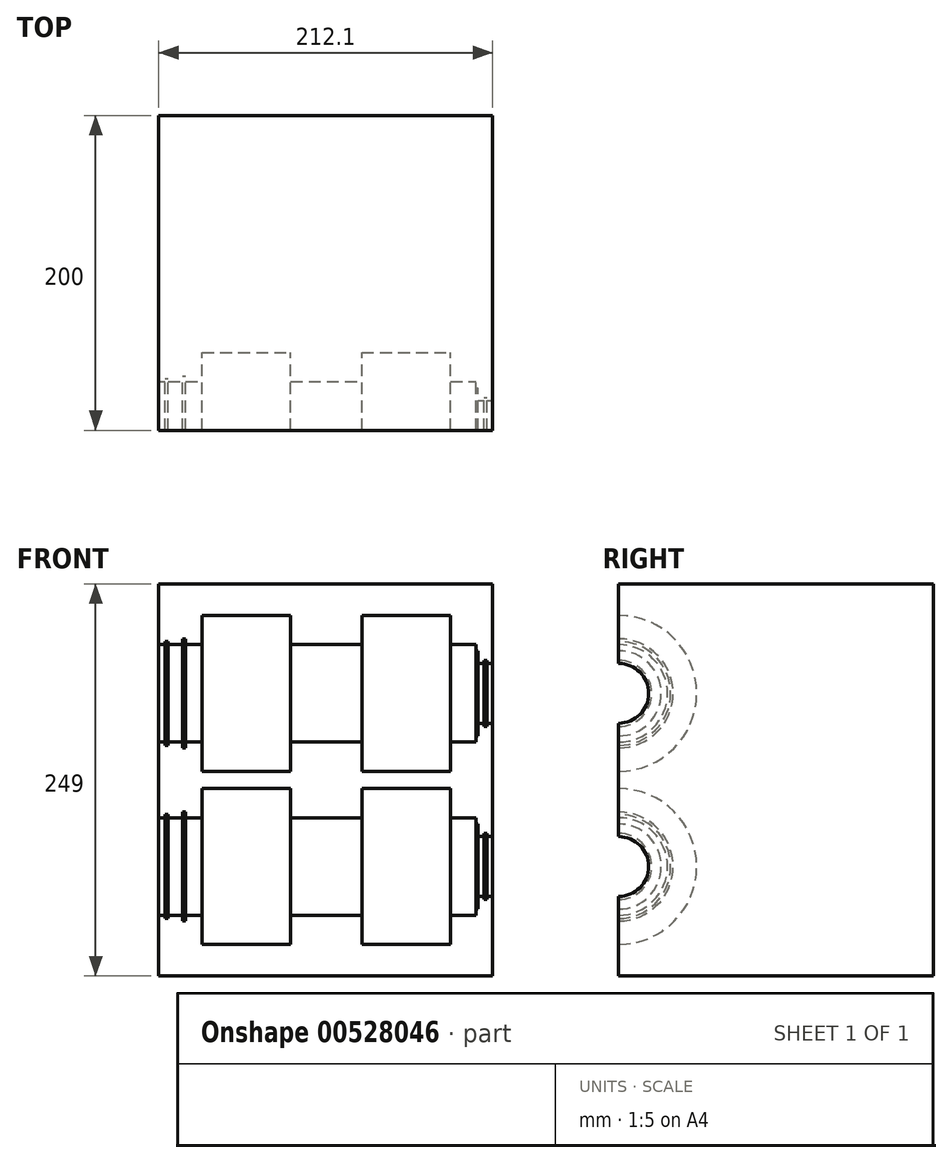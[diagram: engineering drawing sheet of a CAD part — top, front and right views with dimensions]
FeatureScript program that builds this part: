
annotation { "Feature Type Name" : "Feature", "Feature Type Description" : "" }
export const myFeature = defineFeature(function(context is Context, id is Id, definition is map)
    precondition{}
    {
        {
            var Q0;
            Q0=qCreatedBy(makeId("Front.planeOp"),FACE);
            var sketch = newSketch(context, id + "F0", { "sketchPlane" : qUnion([Q0])});
            skLineSegment(sketch, "E0", {"start": v(-107.72, -38.68) * mm, "end": v(-103.72, -38.68) * mm});
            skLineSegment(sketch, "E1", {"start": v(-103.72, -38.68) * mm, "end": v(-103.72, -36.68) * mm});
            skLineSegment(sketch, "E2", {"start": v(-103.72, -36.68) * mm, "end": v(-101.72, -36.68) * mm});
            skLineSegment(sketch, "E3", {"start": v(-101.72, -36.68) * mm, "end": v(-101.72, -38.68) * mm});
            skLineSegment(sketch, "E4", {"start": v(-101.72, -38.68) * mm, "end": v(-92.72, -38.68) * mm});
            skLineSegment(sketch, "E5", {"start": v(-92.72, -38.68) * mm, "end": v(-92.72, -35.08) * mm});
            skLineSegment(sketch, "E6", {"start": v(-92.72, -35.08) * mm, "end": v(-90.72, -35.08) * mm});
            skLineSegment(sketch, "E7", {"start": v(-90.72, -35.08) * mm, "end": v(-90.72, -38.68) * mm});
            skLineSegment(sketch, "E8", {"start": v(-90.72, -38.68) * mm, "end": v(-80.22, -38.68) * mm});
            skLineSegment(sketch, "E9", {"start": v(-80.22, -38.68) * mm, "end": v(-80.22, -20.18) * mm});
            skLineSegment(sketch, "E10", {"start": v(-80.22, -20.18) * mm, "end": v(-23.92, -20.18) * mm});
            skLineSegment(sketch, "E11", {"start": v(-23.92, -20.18) * mm, "end": v(-23.92, -38.68) * mm});
            skLineSegment(sketch, "E12", {"start": v(-23.92, -38.68) * mm, "end": v(21.28, -38.68) * mm});
            skLineSegment(sketch, "E13", {"start": v(21.28, -38.68) * mm, "end": v(21.28, -20.18) * mm});
            skLineSegment(sketch, "E14", {"start": v(21.28, -20.18) * mm, "end": v(77.58, -20.18) * mm});
            skLineSegment(sketch, "E15", {"start": v(77.58, -20.18) * mm, "end": v(77.58, -38.68) * mm});
            skLineSegment(sketch, "E16", {"start": v(77.58, -38.68) * mm, "end": v(93.88, -38.68) * mm});
            skLineSegment(sketch, "E17", {"start": v(93.88, -38.68) * mm, "end": v(93.88, -42.68) * mm});
            skLineSegment(sketch, "E18", {"start": v(93.88, -42.68) * mm, "end": v(94.88, -42.68) * mm});
            skLineSegment(sketch, "E19", {"start": v(94.88, -42.68) * mm, "end": v(94.88, -50.68) * mm});
            skLineSegment(sketch, "E20", {"start": v(94.88, -50.68) * mm, "end": v(98.88, -50.68) * mm});
            skLineSegment(sketch, "E21", {"start": v(98.88, -50.68) * mm, "end": v(98.88, -48.68) * mm});
            skLineSegment(sketch, "E22", {"start": v(98.88, -48.68) * mm, "end": v(100.88, -48.68) * mm});
            skLineSegment(sketch, "E23", {"start": v(100.88, -48.68) * mm, "end": v(100.88, -50.68) * mm});
            skLineSegment(sketch, "E24", {"start": v(100.88, -50.68) * mm, "end": v(104.38, -50.68) * mm});
            skLineSegment(sketch, "E25", {"start": v(-107.72, -69.68) * mm, "end": v(104.38, -69.68) * mm});
            skLineSegment(sketch, "E26", {"start": v(-107.72, 71.32) * mm, "end": v(-103.72, 71.32) * mm});
            skLineSegment(sketch, "E27", {"start": v(-103.72, 71.32) * mm, "end": v(-103.72, 73.32) * mm});
            skLineSegment(sketch, "E28", {"start": v(-103.72, 73.32) * mm, "end": v(-101.72, 73.32) * mm});
            skLineSegment(sketch, "E29", {"start": v(-101.72, 73.32) * mm, "end": v(-101.72, 71.32) * mm});
            skLineSegment(sketch, "E30", {"start": v(-101.72, 71.32) * mm, "end": v(-92.72, 71.32) * mm});
            skLineSegment(sketch, "E31", {"start": v(-92.72, 71.32) * mm, "end": v(-92.72, 74.92) * mm});
            skLineSegment(sketch, "E32", {"start": v(-92.72, 74.92) * mm, "end": v(-90.72, 74.92) * mm});
            skLineSegment(sketch, "E33", {"start": v(-90.72, 74.92) * mm, "end": v(-90.72, 71.32) * mm});
            skLineSegment(sketch, "E34", {"start": v(-90.72, 71.32) * mm, "end": v(-80.22, 71.32) * mm});
            skLineSegment(sketch, "E35", {"start": v(-80.22, 71.32) * mm, "end": v(-80.22, 89.82) * mm});
            skLineSegment(sketch, "E36", {"start": v(-80.22, 89.82) * mm, "end": v(-23.92, 89.82) * mm});
            skLineSegment(sketch, "E37", {"start": v(-23.92, 89.82) * mm, "end": v(-23.92, 71.32) * mm});
            skLineSegment(sketch, "E38", {"start": v(-23.92, 71.32) * mm, "end": v(21.28, 71.32) * mm});
            skLineSegment(sketch, "E39", {"start": v(21.28, 71.32) * mm, "end": v(21.28, 89.82) * mm});
            skLineSegment(sketch, "E40", {"start": v(21.28, 89.82) * mm, "end": v(77.58, 89.82) * mm});
            skLineSegment(sketch, "E41", {"start": v(77.58, 89.82) * mm, "end": v(77.58, 71.32) * mm});
            skLineSegment(sketch, "E42", {"start": v(77.58, 71.32) * mm, "end": v(93.88, 71.32) * mm});
            skLineSegment(sketch, "E43", {"start": v(93.88, 71.32) * mm, "end": v(93.88, 67.32) * mm});
            skLineSegment(sketch, "E44", {"start": v(93.88, 67.32) * mm, "end": v(94.88, 67.32) * mm});
            skLineSegment(sketch, "E45", {"start": v(94.88, 67.32) * mm, "end": v(94.88, 59.32) * mm});
            skLineSegment(sketch, "E46", {"start": v(94.88, 59.32) * mm, "end": v(98.88, 59.32) * mm});
            skLineSegment(sketch, "E47", {"start": v(98.88, 59.32) * mm, "end": v(98.88, 61.32) * mm});
            skLineSegment(sketch, "E48", {"start": v(98.88, 61.32) * mm, "end": v(100.88, 61.32) * mm});
            skLineSegment(sketch, "E49", {"start": v(100.88, 61.32) * mm, "end": v(100.88, 59.32) * mm});
            skLineSegment(sketch, "E50", {"start": v(100.88, 59.32) * mm, "end": v(104.38, 59.32) * mm});
            skLineSegment(sketch, "E51", {"start": v(-107.72, 40.32) * mm, "end": v(104.38, 40.32) * mm});
            skLineSegment(sketch, "E52", {"start": v(-107.72, 71.32) * mm, "end": v(-107.72, 40.32) * mm});
            skLineSegment(sketch, "E53", {"start": v(104.38, 40.32) * mm, "end": v(104.38, 59.32) * mm});
            skLineSegment(sketch, "E54", {"start": v(-107.72, -69.68) * mm, "end": v(-107.72, -38.68) * mm});
            skLineSegment(sketch, "E55", {"start": v(104.38, -69.68) * mm, "end": v(104.38, -50.68) * mm});
            skLineSegment(sketch, "E56", {"start": v(-107.72, 109.82) * mm, "end": v(104.38, 109.82) * mm});
            skLineSegment(sketch, "E57.MirrorCS", {"start": v(-103.72, 7.32) * mm, "end": v(-101.72, 7.32) * mm});
            skLineSegment(sketch, "E58.MirrorCS", {"start": v(98.88, 19.32) * mm, "end": v(100.88, 19.32) * mm});
            skLineSegment(sketch, "E59.MirrorCS", {"start": v(98.88, 21.32) * mm, "end": v(98.88, 19.32) * mm});
            skLineSegment(sketch, "E60.MirrorCS", {"start": v(93.88, 13.32) * mm, "end": v(94.88, 13.32) * mm});
            skLineSegment(sketch, "E61.MirrorCS", {"start": v(-103.72, 9.32) * mm, "end": v(-103.72, 7.32) * mm});
            skLineSegment(sketch, "E62.MirrorCS", {"start": v(93.88, 9.32) * mm, "end": v(93.88, 13.32) * mm});
            skLineSegment(sketch, "E63.MirrorCS", {"start": v(-101.72, 7.32) * mm, "end": v(-101.72, 9.32) * mm});
            skLineSegment(sketch, "E64.MirrorCS", {"start": v(100.88, 21.32) * mm, "end": v(104.38, 21.32) * mm});
            skLineSegment(sketch, "E65.MirrorCS", {"start": v(-92.72, 5.72) * mm, "end": v(-90.72, 5.72) * mm});
            skLineSegment(sketch, "E66.MirrorCS", {"start": v(100.88, 19.32) * mm, "end": v(100.88, 21.32) * mm});
            skLineSegment(sketch, "E67.MirrorCS", {"start": v(-90.72, 5.72) * mm, "end": v(-90.72, 9.32) * mm});
            skLineSegment(sketch, "E68.MirrorCS", {"start": v(-107.72, 9.32) * mm, "end": v(-103.72, 9.32) * mm});
            skLineSegment(sketch, "E69.MirrorCS", {"start": v(94.88, 21.32) * mm, "end": v(98.88, 21.32) * mm});
            skLineSegment(sketch, "E70.MirrorCS", {"start": v(-101.72, 9.32) * mm, "end": v(-92.72, 9.32) * mm});
            skLineSegment(sketch, "E71.MirrorCS", {"start": v(-92.72, 9.32) * mm, "end": v(-92.72, 5.72) * mm});
            skLineSegment(sketch, "E72.MirrorCS", {"start": v(-90.72, 9.32) * mm, "end": v(-80.22, 9.32) * mm});
            skLineSegment(sketch, "E73.MirrorCS", {"start": v(94.88, 13.32) * mm, "end": v(94.88, 21.32) * mm});
            skLineSegment(sketch, "E74.MirrorCS", {"start": v(21.28, 9.32) * mm, "end": v(21.28, -9.18) * mm});
            skLineSegment(sketch, "E75.MirrorCS", {"start": v(-23.92, 9.32) * mm, "end": v(21.28, 9.32) * mm});
            skLineSegment(sketch, "E76.MirrorCS", {"start": v(77.58, 9.32) * mm, "end": v(93.88, 9.32) * mm});
            skLineSegment(sketch, "E77.MirrorCS", {"start": v(-80.22, -9.18) * mm, "end": v(-23.92, -9.18) * mm});
            skLineSegment(sketch, "E78.MirrorCS", {"start": v(-80.22, 9.32) * mm, "end": v(-80.22, -9.18) * mm});
            skLineSegment(sketch, "E79.MirrorCS", {"start": v(-23.92, -9.18) * mm, "end": v(-23.92, 9.32) * mm});
            skLineSegment(sketch, "E80.MirrorCS", {"start": v(77.58, -9.18) * mm, "end": v(77.58, 9.32) * mm});
            skLineSegment(sketch, "E81.MirrorCS", {"start": v(21.28, -9.18) * mm, "end": v(77.58, -9.18) * mm});
            skLineSegment(sketch, "E82", {"start": v(-107.72, 9.32) * mm, "end": v(-107.72, 40.32) * mm});
            skLineSegment(sketch, "E83", {"start": v(104.38, 21.32) * mm, "end": v(104.38, 40.32) * mm});
            skLineSegment(sketch, "E84.MirrorCS", {"start": v(94.88, -96.68) * mm, "end": v(94.88, -88.68) * mm});
            skLineSegment(sketch, "E85.MirrorCS", {"start": v(-92.72, -104.28) * mm, "end": v(-90.72, -104.28) * mm});
            skLineSegment(sketch, "E86.MirrorCS", {"start": v(98.88, -90.68) * mm, "end": v(100.88, -90.68) * mm});
            skLineSegment(sketch, "E87.MirrorCS", {"start": v(94.88, -88.68) * mm, "end": v(98.88, -88.68) * mm});
            skLineSegment(sketch, "E88.MirrorCS", {"start": v(100.88, -90.68) * mm, "end": v(100.88, -88.68) * mm});
            skLineSegment(sketch, "E89.MirrorCS", {"start": v(100.88, -88.68) * mm, "end": v(104.38, -88.68) * mm});
            skLineSegment(sketch, "E90.MirrorCS", {"start": v(-90.72, -104.28) * mm, "end": v(-90.72, -100.68) * mm});
            skLineSegment(sketch, "E91.MirrorCS", {"start": v(-92.72, -100.68) * mm, "end": v(-92.72, -104.28) * mm});
            skLineSegment(sketch, "E92.MirrorCS", {"start": v(98.88, -88.68) * mm, "end": v(98.88, -90.68) * mm});
            skLineSegment(sketch, "E93.MirrorCS", {"start": v(-103.72, -102.68) * mm, "end": v(-101.72, -102.68) * mm});
            skLineSegment(sketch, "E94.MirrorCS", {"start": v(93.88, -100.68) * mm, "end": v(93.88, -96.68) * mm});
            skLineSegment(sketch, "E95.MirrorCS", {"start": v(-103.72, -100.68) * mm, "end": v(-103.72, -102.68) * mm});
            skLineSegment(sketch, "E96.MirrorCS", {"start": v(-101.72, -100.68) * mm, "end": v(-92.72, -100.68) * mm});
            skLineSegment(sketch, "E97.MirrorCS", {"start": v(-90.72, -100.68) * mm, "end": v(-80.22, -100.68) * mm});
            skLineSegment(sketch, "E98.MirrorCS", {"start": v(93.88, -96.68) * mm, "end": v(94.88, -96.68) * mm});
            skLineSegment(sketch, "E99.MirrorCS", {"start": v(-107.72, -100.68) * mm, "end": v(-103.72, -100.68) * mm});
            skLineSegment(sketch, "E100.MirrorCS", {"start": v(-101.72, -102.68) * mm, "end": v(-101.72, -100.68) * mm});
            skLineSegment(sketch, "E101.MirrorCS", {"start": v(77.58, -119.18) * mm, "end": v(77.58, -100.68) * mm});
            skLineSegment(sketch, "E102.MirrorCS", {"start": v(-23.92, -119.18) * mm, "end": v(-23.92, -100.68) * mm});
            skLineSegment(sketch, "E103.MirrorCS", {"start": v(21.28, -100.68) * mm, "end": v(21.28, -119.18) * mm});
            skLineSegment(sketch, "E104.MirrorCS", {"start": v(-80.22, -100.68) * mm, "end": v(-80.22, -119.18) * mm});
            skLineSegment(sketch, "E105.MirrorCS", {"start": v(77.58, -100.68) * mm, "end": v(93.88, -100.68) * mm});
            skLineSegment(sketch, "E106.MirrorCS", {"start": v(-23.92, -100.68) * mm, "end": v(21.28, -100.68) * mm});
            skLineSegment(sketch, "E107.MirrorCS", {"start": v(21.28, -119.18) * mm, "end": v(77.58, -119.18) * mm});
            skLineSegment(sketch, "E108.MirrorCS", {"start": v(-80.22, -119.18) * mm, "end": v(-23.92, -119.18) * mm});
            skLineSegment(sketch, "E109", {"start": v(-107.72, -100.68) * mm, "end": v(-107.72, -69.68) * mm});
            skLineSegment(sketch, "E110", {"start": v(104.38, -88.68) * mm, "end": v(104.38, -69.68) * mm});
            skLineSegment(sketch, "E111", {"start": v(-107.72, 109.82) * mm, "end": v(-107.72, 71.32) * mm});
            skLineSegment(sketch, "E112", {"start": v(104.38, 109.82) * mm, "end": v(104.38, 59.32) * mm});
            skLineSegment(sketch, "E113", {"start": v(-107.72, -38.68) * mm, "end": v(-107.72, 9.32) * mm});
            skLineSegment(sketch, "E114", {"start": v(104.38, -50.68) * mm, "end": v(104.38, 21.32) * mm});
            skLineSegment(sketch, "E115", {"start": v(-107.72, -100.68) * mm, "end": v(-107.72, -139.18) * mm});
            skLineSegment(sketch, "E116", {"start": v(-107.72, -139.18) * mm, "end": v(104.38, -139.18) * mm});
            skLineSegment(sketch, "E117", {"start": v(104.38, -139.18) * mm, "end": v(104.38, -88.68) * mm});
            skSolve(sketch);
        }
        {
            var Q0;
            Q0=makeQuery(id+"F0.imprint","IMPRINT",FACE,{"disambiguationData":[TD([[makeQuery(id+"F0.imprint","IMPRINT",EDGE,{"derivedFrom":sQuery(id+"F0.wireOp",EDGE,"E26")}),-1.0]])]});
            var Q1;
            Q1=makeQuery(id+"F0.imprint","IMPRINT",FACE,{"disambiguationData":[TD([[makeQuery(id+"F0.imprint","IMPRINT",EDGE,{"derivedFrom":sQuery(id+"F0.wireOp",EDGE,"E26")}),1.0]])]});
            var Q2;
            Q2=makeQuery(id+"F0.imprint","IMPRINT",FACE,{"disambiguationData":[TD([[makeQuery(id+"F0.imprint","IMPRINT",EDGE,{"derivedFrom":sQuery(id+"F0.wireOp",EDGE,"E51")}),-1.0]])]});
            var Q3;
            Q3=makeQuery(id+"F0.imprint","IMPRINT",FACE,{"disambiguationData":[TD([[makeQuery(id+"F0.imprint","IMPRINT",EDGE,{"derivedFrom":sQuery(id+"F0.wireOp",EDGE,"E0")}),1.0]])]});
            var Q4;
            Q4=makeQuery(id+"F0.imprint","IMPRINT",FACE,{"disambiguationData":[TD([[makeQuery(id+"F0.imprint","IMPRINT",EDGE,{"derivedFrom":sQuery(id+"F0.wireOp",EDGE,"E0")}),-1.0]])]});
            var Q5;
            Q5=makeQuery(id+"F0.imprint","IMPRINT",FACE,{"disambiguationData":[TD([[makeQuery(id+"F0.imprint","IMPRINT",EDGE,{"derivedFrom":sQuery(id+"F0.wireOp",EDGE,"E25")}),-1.0]])]});
            var Q6;
            Q6=makeQuery(id+"F0.imprint","IMPRINT",FACE,{"disambiguationData":[TD([[makeQuery(id+"F0.imprint","IMPRINT",EDGE,{"derivedFrom":sQuery(id+"F0.wireOp",EDGE,"E84.MirrorCS")}),-1.0]])]});
            var Q7;
            Q7=sQuery(id+"F0.wireOp",EDGE,"E56");
            var Q8;
            Q8=sQuery(id+"F0.wireOp",EDGE,"E111");
            var Q9;
            Q9=sQuery(id+"F0.wireOp",EDGE,"E52");
            var Q10;
            Q10=sQuery(id+"F0.wireOp",EDGE,"E82");
            var Q11;
            Q11=sQuery(id+"F0.wireOp",EDGE,"E113");
            var Q12;
            Q12=sQuery(id+"F0.wireOp",EDGE,"E54");
            var Q13;
            Q13=sQuery(id+"F0.wireOp",EDGE,"E109");
            var Q14;
            Q14=sQuery(id+"F0.wireOp",EDGE,"E115");
            var Q15;
            Q15=sQuery(id+"F0.wireOp",EDGE,"E116");
            var Q16;
            Q16=sQuery(id+"F0.wireOp",EDGE,"E117");
            var Q17;
            Q17=sQuery(id+"F0.wireOp",EDGE,"E110");
            var Q18;
            Q18=sQuery(id+"F0.wireOp",EDGE,"E55");
            var Q19;
            Q19=sQuery(id+"F0.wireOp",EDGE,"E114");
            var Q20;
            Q20=sQuery(id+"F0.wireOp",EDGE,"E83");
            var Q21;
            Q21=sQuery(id+"F0.wireOp",EDGE,"E53");
            var Q22;
            Q22=sQuery(id+"F0.wireOp",EDGE,"E112");
            extrude(context, id + "F1", {"entities" : qUnion([Q0, Q1, Q2, Q3, Q4, Q5, Q6]), "surfaceEntities" : qUnion([Q7, Q8, Q9, Q10, Q11, Q12, Q13, Q14, Q15, Q16, Q17, Q18, Q19, Q20, Q21, Q22]), "oppositeDirection" : true, "depth" : 200 * mm, "offsetDistance" : 25 * mm});
        }
        {
            var Q0;
            Q0=makeQuery(id+"F0.imprint","IMPRINT",FACE,{"disambiguationData":[TD([[makeQuery(id+"F0.imprint","IMPRINT",EDGE,{"derivedFrom":sQuery(id+"F0.wireOp",EDGE,"E26")}),-1.0]])]});
            var Q1;
            Q1=sQuery(id+"F0.wireOp",EDGE,"E51");
            revolve(context, id + "F2", {"operationType" : NewBodyOperationType.REMOVE, "entities" : qUnion([Q0]), "axis" : qUnion([Q1]), "revolveType" : RevolveType.FULL, "oppositeDirection" : true});
        }
        {
            var Q0;
            Q0=makeQuery(id+"F0.imprint","IMPRINT",FACE,{"disambiguationData":[TD([[makeQuery(id+"F0.imprint","IMPRINT",EDGE,{"derivedFrom":sQuery(id+"F0.wireOp",EDGE,"E0")}),-1.0]])]});
            var Q1;
            Q1=sQuery(id+"F0.wireOp",EDGE,"E25");
            revolve(context, id + "F3", {"operationType" : NewBodyOperationType.REMOVE, "entities" : qUnion([Q0]), "axis" : qUnion([Q1]), "revolveType" : RevolveType.FULL, "oppositeDirection" : true});
        }
    });
